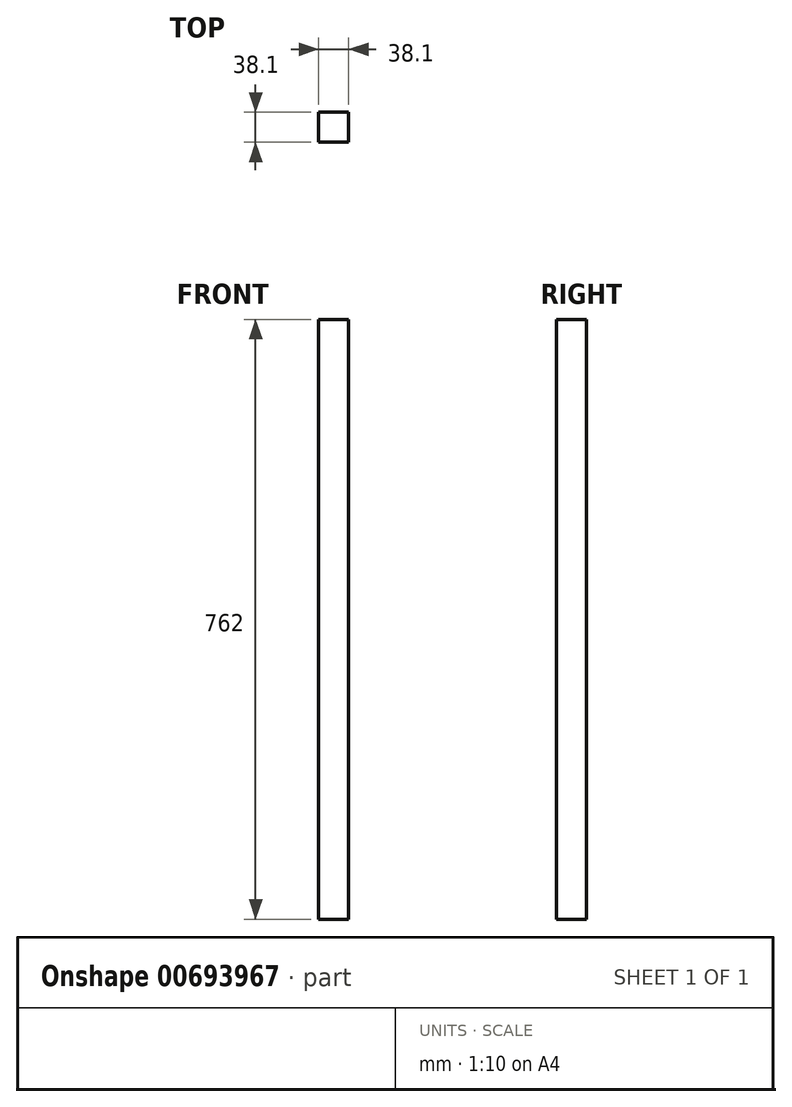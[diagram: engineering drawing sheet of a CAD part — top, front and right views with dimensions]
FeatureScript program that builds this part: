
annotation { "Feature Type Name" : "Feature", "Feature Type Description" : "" }
export const myFeature = defineFeature(function(context is Context, id is Id, definition is map)
    precondition{}
    {
        {
            var Q0;
            Q0=qCreatedBy(makeId("Top.planeOp"),FACE);
            var sketch = newSketch(context, id + "F0", { "sketchPlane" : qUnion([Q0])});
            skLineSegment(sketch, "E0.bottom", {"start": v(0, 0) * mm, "end": v(38.1, 0) * mm});
            skLineSegment(sketch, "E0.top", {"start": v(0, -38.1) * mm, "end": v(38.1, -38.1) * mm});
            skLineSegment(sketch, "E0.left", {"start": v(0, 0) * mm, "end": v(0, -38.1) * mm});
            skLineSegment(sketch, "E0.right", {"start": v(38.1, 0) * mm, "end": v(38.1, -38.1) * mm});
            skSolve(sketch);
        }
        {
            var Q0;
            Q0 = qSketchRegion(id + "F0", true);
            extrude(context, id + "F1", {"entities" : qUnion([Q0]), "depth" : 762 * mm, "offsetDistance" : 25.4 * mm});
        }
    });
